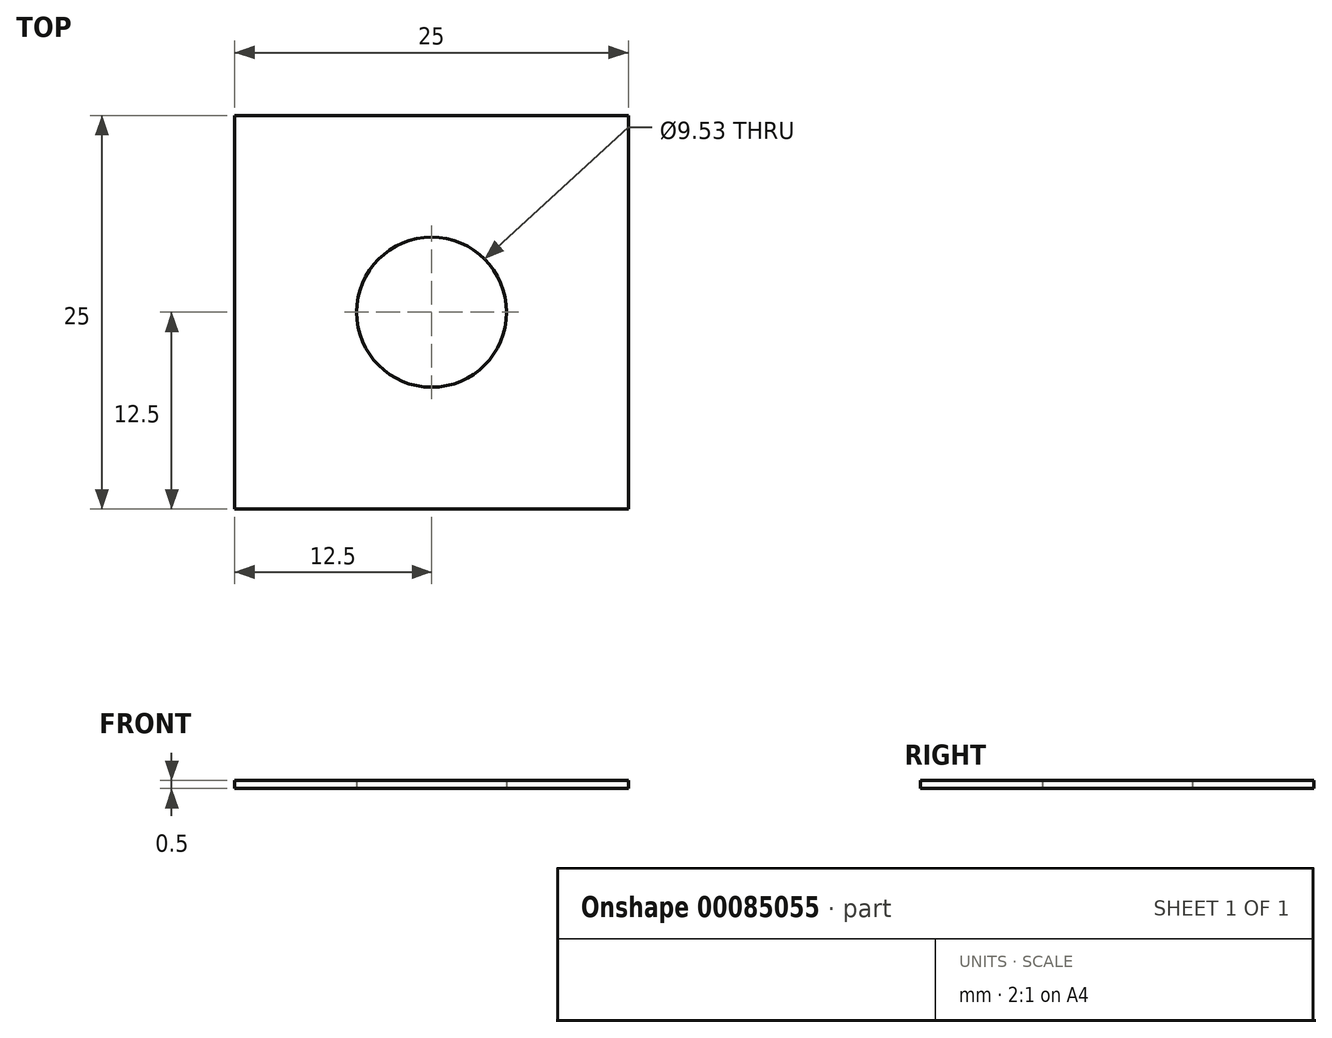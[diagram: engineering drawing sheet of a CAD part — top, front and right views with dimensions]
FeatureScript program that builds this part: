
annotation { "Feature Type Name" : "Feature", "Feature Type Description" : "" }
export const myFeature = defineFeature(function(context is Context, id is Id, definition is map)
    precondition{}
    {
        {
            var Q0;
            Q0=qCreatedBy(makeId("Top.planeOp"),FACE);
            var sketch = newSketch(context, id + "F0", { "sketchPlane" : qUnion([Q0])});
            skLineSegment(sketch, "E0.bottom", {"start": v(12.5, -12.5) * mm, "end": v(-12.5, -12.5) * mm});
            skLineSegment(sketch, "E0.top", {"start": v(12.5, 12.5) * mm, "end": v(-12.5, 12.5) * mm});
            skLineSegment(sketch, "E0.left", {"start": v(12.5, -12.5) * mm, "end": v(12.5, 12.5) * mm});
            skLineSegment(sketch, "E0.right", {"start": v(-12.5, -12.5) * mm, "end": v(-12.5, 12.5) * mm});
            skPoint(sketch, "E0.middle", {"position": v(0, 0) * mm});
            skCircle(sketch, "E1", {"center": v(0, 0) * mm, "radius": 4.76 * mm});
            skSolve(sketch);
        }
        {
            var Q0;
            Q0 = qSketchRegion(id + "F0", true);
            extrude(context, id + "F1", {"entities" : qUnion([Q0]), "depth" : .5 * mm});
        }
    });
